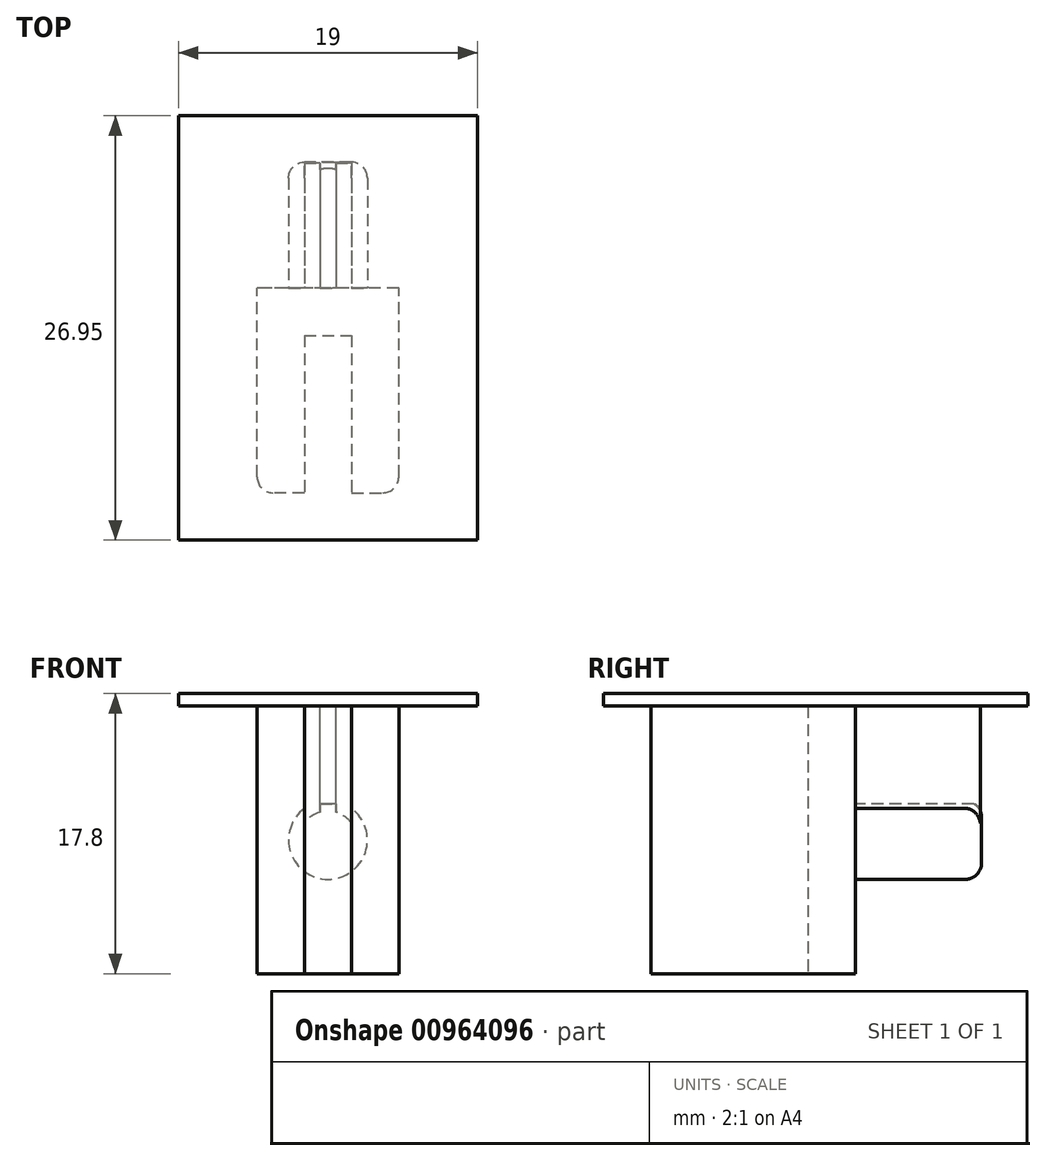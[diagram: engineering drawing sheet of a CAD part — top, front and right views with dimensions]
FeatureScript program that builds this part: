
annotation { "Feature Type Name" : "Feature", "Feature Type Description" : "" }
export const myFeature = defineFeature(function(context is Context, id is Id, definition is map)
    precondition{}
    {
        {
            var Q0;
            Q0=qCreatedBy(makeId("Top.planeOp"),FACE);
            var sketch = newSketch(context, id + "F0", { "sketchPlane" : qUnion([Q0])});
            skLineSegment(sketch, "E0", {"start": v(0, 0) * mm, "end": v(1.5, 0) * mm});
            skLineSegment(sketch, "E1", {"start": v(1.5, 0) * mm, "end": v(1.5, -10) * mm});
            skLineSegment(sketch, "E2", {"start": v(1.5, -10) * mm, "end": v(4.5, -10) * mm});
            skLineSegment(sketch, "E3", {"start": v(0, 0) * mm, "end": v(0, 3) * mm});
            skLineSegment(sketch, "E4", {"start": v(4.5, -10) * mm, "end": v(4.5, 3) * mm});
            skLineSegment(sketch, "E5", {"start": v(4.5, 3) * mm, "end": v(0, 3) * mm});
            skSolve(sketch);
        }
        {
            var Q0;
            Q0=makeQuery(id+"F0.imprint","IMPRINT",FACE,{"disambiguationData":[TD([[makeQuery(id+"F0.imprint","IMPRINT",EDGE,{"derivedFrom":sQuery(id+"F0.wireOp",EDGE,"E0")}),1.0]])]});
            extrude(context, id + "F1", {"entities" : qUnion([Q0]), "depth" : 17 * mm, "offsetDistance" : 25 * mm});
        }
        {
            var Q0;
            Q0=makeQuery(id+"F1.opExtrude","SWEPT_BODY",BODY,{"disambiguationData":[OSD([sQuery(id+"F0.wireOp",EDGE,"E0"),sQuery(id+"F0.wireOp",EDGE,"E1"),sQuery(id+"F0.wireOp",EDGE,"E2"),sQuery(id+"F0.wireOp",EDGE,"E3"),sQuery(id+"F0.wireOp",EDGE,"E4"),sQuery(id+"F0.wireOp",EDGE,"E5")])]});
            var Q1;
            Q1=qCreatedBy(makeId("Right.planeOp"),FACE);
            mirror(context, id + "F2", {"operationType" : NewBodyOperationType.ADD, "entities" : qUnion([Q0]), "mirrorPlane" : qUnion([Q1])});
        }
        {
            var Q0;
            {var subQ0=makeQuery(id+"F1.opExtrude","SWEPT_FACE",FACE,{"disambiguationData":[OSD([sQuery(id+"F0.wireOp",EDGE,"E5")])]});Q0=makeQuery(id+"F2.boolean.opBoolean","MERGE",FACE,{"derivedFrom":[subQ0,makeQuery(id+"F2.opPattern","COPY",FACE,{"derivedFrom":subQ0,"instanceName":"1"})]});}
            var sketch = newSketch(context, id + "F3", { "sketchPlane" : qUnion([Q0])});
            skLineSegment(sketch, "E6", {"start": v(0, 17) * mm, "end": v(0, 0) * mm, "construction": true});
            skCircle(sketch, "E7", {"center": v(0, 8.5) * mm, "radius": 2.5 * mm});
            skLineSegment(sketch, "E8", {"start": v(0.98, 10.8) * mm, "end": v(-0.98, 10.8) * mm});
            skSolve(sketch);
        }
        {
            var Q0;
            {var subQ0=sQuery(id+"F3.wireOp",EDGE,"E8");Q0=makeQuery(id+"F3.imprint","IMPRINT",FACE,{"disambiguationData":[TD([[makeQuery(id+"F3.imprint","IMPRINT",EDGE,{"derivedFrom":subQ0}),1.0]])]});}
            extrude(context, id + "F4", {"entities" : qUnion([Q0]), "operationType" : NewBodyOperationType.ADD, "depth" : 8 * mm, "offsetDistance" : 25 * mm});
        }
        {
            var Q0;
            Q0=makeQuery(id+"F4.opExtrude","CAP_EDGE",EDGE,{"disambiguationData":[OSD([sQuery(id+"F3.wireOp",EDGE,"E7")])],"isStart":false});
            fillet(context, id + "F5", {"entities" : qUnion([Q0]), "radius" : 1 * mm, "tangentPropagation" : true, "allowEdgeOverflow" : false});
        }
        {
            var Q0;
            Q0=makeQuery(id+"F2.opPattern","COPY",EDGE,{"derivedFrom":makeQuery(id+"F1.opExtrude","SWEPT_EDGE",EDGE,{"disambiguationData":[OSD([sQuery(id+"F0.wireOp",EDGE,"E2"),sQuery(id+"F0.wireOp",EDGE,"E4")])]}),"instanceName":"1"});
            var Q1;
            Q1=makeQuery(id+"F1.opExtrude","SWEPT_EDGE",EDGE,{"disambiguationData":[OSD([sQuery(id+"F0.wireOp",EDGE,"E2"),sQuery(id+"F0.wireOp",EDGE,"E4")])]});
            fillet(context, id + "F6", {"entities" : qUnion([Q0, Q1]), "radius" : 1 * mm, "tangentPropagation" : true, "allowEdgeOverflow" : false});
        }
        {
            var Q0;
            {var subQ0=makeQuery(id+"F1.opExtrude","CAP_FACE",FACE,{"disambiguationData":[OSD([sQuery(id+"F0.wireOp",EDGE,"E0"),sQuery(id+"F0.wireOp",EDGE,"E1"),sQuery(id+"F0.wireOp",EDGE,"E2"),sQuery(id+"F0.wireOp",EDGE,"E3"),sQuery(id+"F0.wireOp",EDGE,"E4"),sQuery(id+"F0.wireOp",EDGE,"E5")])],"isStart":false});Q0=makeQuery(id+"F2.boolean.opBoolean","MERGE",FACE,{"derivedFrom":[subQ0,makeQuery(id+"F2.opPattern","COPY",FACE,{"derivedFrom":subQ0,"instanceName":"1"})]});}
            var sketch = newSketch(context, id + "F7", { "sketchPlane" : qUnion([Q0])});
            skLineSegment(sketch, "E9", {"start": v(6.5, -10) * mm, "end": v(3.5, -10) * mm});
            skLineSegment(sketch, "E10", {"start": v(3.5, -10) * mm, "end": v(-3.5, -10) * mm});
            skLineSegment(sketch, "E11", {"start": v(-3.5, -10) * mm, "end": v(-6.5, -10) * mm});
            skLineSegment(sketch, "E12", {"start": v(0, 10.95) * mm, "end": v(-6.5, 10.95) * mm});
            skLineSegment(sketch, "E13", {"start": v(-6.5, 10.95) * mm, "end": v(-6.5, -10) * mm});
            skLineSegment(sketch, "E14", {"start": v(0, 10.95) * mm, "end": v(6.5, 10.95) * mm});
            skLineSegment(sketch, "E15", {"start": v(6.5, 10.95) * mm, "end": v(6.5, -10) * mm});
            skLineSegment(sketch, "E16.0", {"start": v(0, 13.95) * mm, "end": v(-9.5, 13.95) * mm});
            skLineSegment(sketch, "E16.1", {"start": v(-9.5, 13.95) * mm, "end": v(-9.5, -13) * mm});
            skLineSegment(sketch, "E16.2", {"start": v(9.5, 13.95) * mm, "end": v(9.5, -13) * mm});
            skLineSegment(sketch, "E16.3", {"start": v(9.5, -13) * mm, "end": v(3.5, -13) * mm});
            skLineSegment(sketch, "E16.4", {"start": v(3.5, -13) * mm, "end": v(-3.5, -13) * mm});
            skLineSegment(sketch, "E16.5", {"start": v(0, 13.95) * mm, "end": v(9.5, 13.95) * mm});
            skLineSegment(sketch, "E16.6", {"start": v(-3.5, -13) * mm, "end": v(-9.5, -13) * mm});
            skSolve(sketch);
        }
        {
            var Q0;
            Q0=makeQuery(id+"F7.imprint","IMPRINT",FACE,{"disambiguationData":[TD([[makeQuery(id+"F7.imprint","IMPRINT",EDGE,{"derivedFrom":sQuery(id+"F7.wireOp",EDGE,"E9")}),-1.0]])]});
            var Q1;
            {var subQ0=sQuery(id+"F0.wireOp",EDGE,"E1");var subQ1=makeQuery(id+"F1.opExtrude","CAP_EDGE",EDGE,{"disambiguationData":[OSD([subQ0])],"isStart":false});Q1=makeQuery(id+"F7.imprint","IMPRINT",FACE,{"disambiguationData":[TD([[makeQuery(id+"F7.imprint","IMPRINT",EDGE,{"derivedFrom":subQ1}),1.0]])]});}
            var Q2;
            {var subQ1=makeQuery(id+"F1.opExtrude","CAP_EDGE",EDGE,{"disambiguationData":[OSD([sQuery(id+"F0.wireOp",EDGE,"E1")])],"isStart":false});Q2=makeQuery(id+"F7.imprint","IMPRINT",FACE,{"disambiguationData":[TD([[makeQuery(id+"F7.imprint","IMPRINT",EDGE,{"derivedFrom":subQ1}),-1.0]])]});}
            var Q3;
            {var subQ1=sQuery(id+"F7.wireOp",EDGE,"E9");Q3=makeQuery(id+"F7.imprint","IMPRINT",FACE,{"disambiguationData":[TD([[makeQuery(id+"F7.imprint","IMPRINT",EDGE,{"derivedFrom":subQ1}),1.0]])]});}
            extrude(context, id + "F8", {"entities" : qUnion([Q0, Q1, Q2, Q3]), "operationType" : NewBodyOperationType.ADD, "depth" : 0.8 * mm, "offsetDistance" : 25 * mm});
        }
        {
            var Q0;
            Q0=makeQuery(id+"F8.opExtrude","CAP_FACE",FACE,{"disambiguationData":[OSD([sQuery(id+"F7.wireOp",EDGE,"E16.0"),sQuery(id+"F7.wireOp",EDGE,"E16.1"),sQuery(id+"F7.wireOp",EDGE,"E16.2"),sQuery(id+"F7.wireOp",EDGE,"E16.3"),sQuery(id+"F7.wireOp",EDGE,"E16.4"),sQuery(id+"F7.wireOp",EDGE,"E16.5"),sQuery(id+"F7.wireOp",EDGE,"E16.6")])],"isStart":true});
            var sketch = newSketch(context, id + "F9", { "sketchPlane" : qUnion([Q0])});
            skLineSegment(sketch, "E17", {"start": v(0, -3) * mm, "end": v(0, -10.94) * mm, "construction": true});
            skCircle(sketch, "E18", {"center": v(0, -10.94) * mm, "radius": 1 * mm, "construction": true});
            skLineSegment(sketch, "E19", {"start": v(1, -10.94) * mm, "end": v(1.5, -10.94) * mm});
            skLineSegment(sketch, "E20", {"start": v(1, -10.94) * mm, "end": v(0.5, -10.94) * mm});
            skLineSegment(sketch, "E21", {"start": v(0.5, -10.94) * mm, "end": v(0.5, -3) * mm});
            skLineSegment(sketch, "E22", {"start": v(1.5, -10.94) * mm, "end": v(1.5, -3) * mm});
            skLineSegment(sketch, "E23", {"start": v(1.5, -3) * mm, "end": v(0.5, -3) * mm});
            skLineSegment(sketch, "E24.MirrorCS", {"start": v(-1, -10.94) * mm, "end": v(-0.5, -10.94) * mm});
            skLineSegment(sketch, "E25.MirrorCS", {"start": v(-1, -10.94) * mm, "end": v(-1.5, -10.94) * mm});
            skLineSegment(sketch, "E26.MirrorCS", {"start": v(-1.5, -10.94) * mm, "end": v(-1.5, -3) * mm});
            skLineSegment(sketch, "E27.MirrorCS", {"start": v(-1.5, -3) * mm, "end": v(-0.5, -3) * mm});
            skLineSegment(sketch, "E28.MirrorCS", {"start": v(-0.5, -10.94) * mm, "end": v(-0.5, -3) * mm});
            skSolve(sketch);
        }
        {
            var Q0;
            Q0=makeQuery(id+"F9.imprint","IMPRINT",FACE,{"disambiguationData":[TD([[makeQuery(id+"F9.imprint","IMPRINT",EDGE,{"derivedFrom":sQuery(id+"F9.wireOp",EDGE,"E19")}),1.0]])]});
            var Q1;
            Q1=makeQuery(id+"F9.imprint","IMPRINT",FACE,{"disambiguationData":[TD([[makeQuery(id+"F9.imprint","IMPRINT",EDGE,{"derivedFrom":sQuery(id+"F9.wireOp",EDGE,"E24.MirrorCS")}),1.0]])]});
            extrude(context, id + "F10", {"entities" : qUnion([Q0, Q1]), "operationType" : NewBodyOperationType.ADD, "endBound" : BoundingType.UP_TO_NEXT, "depth" : 25 * mm, "offsetDistance" : 25 * mm});
        }
    });
